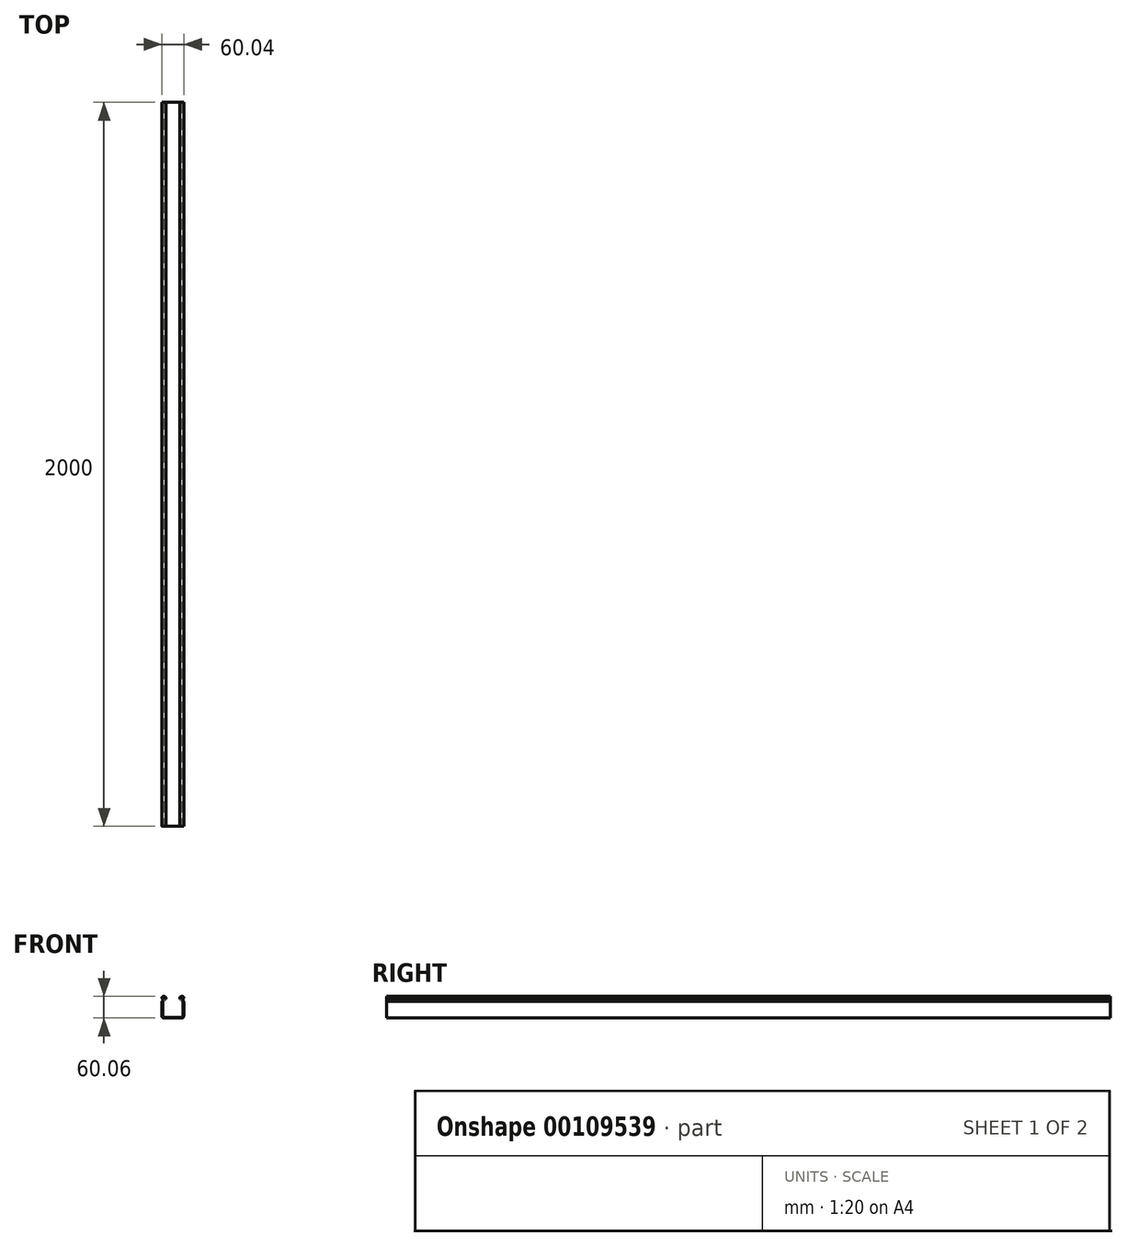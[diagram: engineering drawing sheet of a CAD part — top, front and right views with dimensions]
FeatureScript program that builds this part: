
annotation { "Feature Type Name" : "Feature", "Feature Type Description" : "" }
export const myFeature = defineFeature(function(context is Context, id is Id, definition is map)
    precondition{}
    {
        {
            var Q0;
            Q0=qCreatedBy(makeId("Front.planeOp"),FACE);
            var sketch = newSketch(context, id + "F0", { "sketchPlane" : qUnion([Q0])});
            skLineSegment(sketch, "E0", {"start": v(0, 0) * mm, "end": v(25, 0) * mm});
            skLineSegment(sketch, "E1", {"start": v(30, 5) * mm, "end": v(30, 46) * mm});
            skLineSegment(sketch, "E2", {"start": v(30, 46) * mm, "end": v(30, 50) * mm, "construction": true});
            skLineSegment(sketch, "E3", {"start": v(30, 50) * mm, "end": v(30, 60) * mm, "construction": true});
            skLineSegment(sketch, "E4", {"start": v(30, 46) * mm, "end": v(27, 46) * mm, "construction": true});
            skLineSegment(sketch, "E5", {"start": v(27, 46) * mm, "end": v(27, 50) * mm, "construction": true});
            skLineSegment(sketch, "E6", {"start": v(30, 46) * mm, "end": v(27, 50) * mm});
            skLineSegment(sketch, "E7", {"start": v(30, 60) * mm, "end": v(24, 60) * mm, "construction": true});
            skLineSegment(sketch, "E8.5", {"start": v(28, 45.33) * mm, "end": v(24.7, 49.73) * mm});
            skLineSegment(sketch, "E8.6", {"start": v(28, 5) * mm, "end": v(28, 45.33) * mm});
            skLineSegment(sketch, "E8.7", {"start": v(0, 2) * mm, "end": v(25, 2) * mm});
            skPoint(sketch, "E9.visualSharp", {"position": v(30, 0) * mm});
            skArc(sketch, "E9.filletArc", {"start": v(25, 0) * mm, "mid": v(28.54, 1.46) * mm, "end": v(30, 5) * mm});
            skPoint(sketch, "E10.visualSharp", {"position": v(28, 2) * mm});
            skArc(sketch, "E10.filletArc", {"start": v(25, 2) * mm, "mid": v(27.12, 2.88) * mm, "end": v(28, 5) * mm});
            skLineSegment(sketch, "E11.MirrorCS", {"start": v(0, 0) * mm, "end": v(-25, 0) * mm});
            skLineSegment(sketch, "E12.MirrorCS", {"start": v(0, 2) * mm, "end": v(-25, 2) * mm});
            skLineSegment(sketch, "E13.MirrorCS", {"start": v(-27.74, 56.8) * mm, "end": v(-28.52, 58.63) * mm, "construction": true});
            skLineSegment(sketch, "E14.MirrorCS", {"start": v(-27, 57) * mm, "end": v(-30, 57) * mm, "construction": true});
            skLineSegment(sketch, "E15.MirrorCS", {"start": v(-30, 46) * mm, "end": v(-27, 50) * mm});
            skLineSegment(sketch, "E16.MirrorCS", {"start": v(-28, 45.33) * mm, "end": v(-24.7, 49.73) * mm});
            skLineSegment(sketch, "E17.MirrorCS", {"start": v(-30, 46) * mm, "end": v(-27, 46) * mm, "construction": true});
            skArc(sketch, "E18.MirrorCS", {"start": v(-25, 2) * mm, "mid": v(-27.12, 2.88) * mm, "end": v(-28, 5) * mm});
            skLineSegment(sketch, "E19.MirrorCS", {"start": v(-27, 46) * mm, "end": v(-27, 50) * mm, "construction": true});
            skLineSegment(sketch, "E20.MirrorCS", {"start": v(-30, 46) * mm, "end": v(-30, 50) * mm, "construction": true});
            skLineSegment(sketch, "E21.MirrorCS", {"start": v(-30, 60) * mm, "end": v(-24, 60) * mm, "construction": true});
            skArc(sketch, "E22.MirrorCS", {"start": v(-25, 0) * mm, "mid": v(-28.54, 1.46) * mm, "end": v(-30, 5) * mm});
            skPoint(sketch, "E23.MirrorP", {"position": v(-30, 0) * mm});
            skLineSegment(sketch, "E24.MirrorCS", {"start": v(-30, 5) * mm, "end": v(-30, 46) * mm});
            skLineSegment(sketch, "E25.MirrorCS", {"start": v(-28, 5) * mm, "end": v(-28, 45.33) * mm});
            skPoint(sketch, "E26.MirrorP", {"position": v(-28, 2) * mm});
            skLineSegment(sketch, "E27.MirrorCS", {"start": v(-27, 50) * mm, "end": v(-27, 57) * mm, "construction": true});
            skLineSegment(sketch, "E28.MirrorCS", {"start": v(-30, 50) * mm, "end": v(-30, 60) * mm, "construction": true});
            skLineSegment(sketch, "E29", {"start": v(-27, 50) * mm, "end": v(-27.8, 51.86) * mm});
            skArc(sketch, "E30.filletArc", {"start": v(-27.8, 51.86) * mm, "mid": v(-28, 52.23) * mm, "end": v(-28.27, 52.54) * mm});
            skPoint(sketch, "E31.third.point", {"position": v(-19.08, 52.63) * mm});
            skArc(sketch, "E32.trimOffspring", {"start": v(-30, 57) * mm, "mid": v(-29.65, 54.57) * mm, "end": v(-28.27, 52.54) * mm});
            skArc(sketch, "E33.trimOffspring", {"start": v(-19.08, 52.63) * mm, "mid": v(-22.61, 59.63) * mm, "end": v(-30, 57) * mm});
            skArc(sketch, "E34.0", {"start": v(-25.96, 52.65) * mm, "mid": v(-26.36, 53.38) * mm, "end": v(-26.9, 54) * mm});
            skLineSegment(sketch, "E34.1", {"start": v(-25.16, 50.79) * mm, "end": v(-25.96, 52.65) * mm});
            skArc(sketch, "E35.0", {"start": v(-28.01, 56.4) * mm, "mid": v(-27.7, 55.1) * mm, "end": v(-26.9, 54) * mm});
            skArc(sketch, "E35.1", {"start": v(-21.02, 53.13) * mm, "mid": v(-23.15, 57.69) * mm, "end": v(-28.01, 56.4) * mm});
            skLineSegment(sketch, "E36", {"start": v(-21.02, 53.13) * mm, "end": v(-19.08, 52.63) * mm});
            skLineSegment(sketch, "E37", {"start": v(-25.96, 52.65) * mm, "end": v(-24.7, 49.73) * mm});
            skArc(sketch, "E38.MirrorCS", {"start": v(25.96, 52.65) * mm, "mid": v(26.36, 53.38) * mm, "end": v(26.9, 54) * mm});
            skLineSegment(sketch, "E39.MirrorCS", {"start": v(27, 57) * mm, "end": v(30, 57) * mm, "construction": true});
            skLineSegment(sketch, "E40.MirrorCS", {"start": v(27, 50) * mm, "end": v(27.8, 51.86) * mm});
            skArc(sketch, "E41.MirrorCS", {"start": v(27.8, 51.86) * mm, "mid": v(28, 52.23) * mm, "end": v(28.27, 52.54) * mm});
            skLineSegment(sketch, "E42.MirrorCS", {"start": v(27, 50) * mm, "end": v(27, 57) * mm, "construction": true});
            skLineSegment(sketch, "E43.MirrorCS", {"start": v(21.02, 53.13) * mm, "end": v(19.08, 52.63) * mm});
            skArc(sketch, "E44.MirrorCS", {"start": v(28.01, 56.4) * mm, "mid": v(27.7, 55.1) * mm, "end": v(26.9, 54) * mm});
            skLineSegment(sketch, "E45.MirrorCS", {"start": v(27.74, 56.8) * mm, "end": v(28.52, 58.63) * mm, "construction": true});
            skLineSegment(sketch, "E46.MirrorCS", {"start": v(25.16, 50.79) * mm, "end": v(25.96, 52.65) * mm});
            skLineSegment(sketch, "E47.MirrorCS", {"start": v(25.96, 52.65) * mm, "end": v(24.7, 49.73) * mm});
            skPoint(sketch, "E48.MirrorP", {"position": v(19.08, 52.63) * mm});
            skArc(sketch, "E49.MirrorCS", {"start": v(21.02, 53.13) * mm, "mid": v(23.15, 57.69) * mm, "end": v(28.01, 56.4) * mm});
            skArc(sketch, "E50.MirrorCS", {"start": v(19.08, 52.63) * mm, "mid": v(22.61, 59.63) * mm, "end": v(30, 57) * mm});
            skArc(sketch, "E51.MirrorCS", {"start": v(30, 57) * mm, "mid": v(29.65, 54.57) * mm, "end": v(28.27, 52.54) * mm});
            skSolve(sketch);
        }
        {
            var Q0;
            Q0=qSketchRegion(id+"F0",true);
            extrude(context, id + "F1", {"entities" : qUnion([Q0]), "oppositeDirection" : true, "depth" : 2000 * mm});
        }
    });
